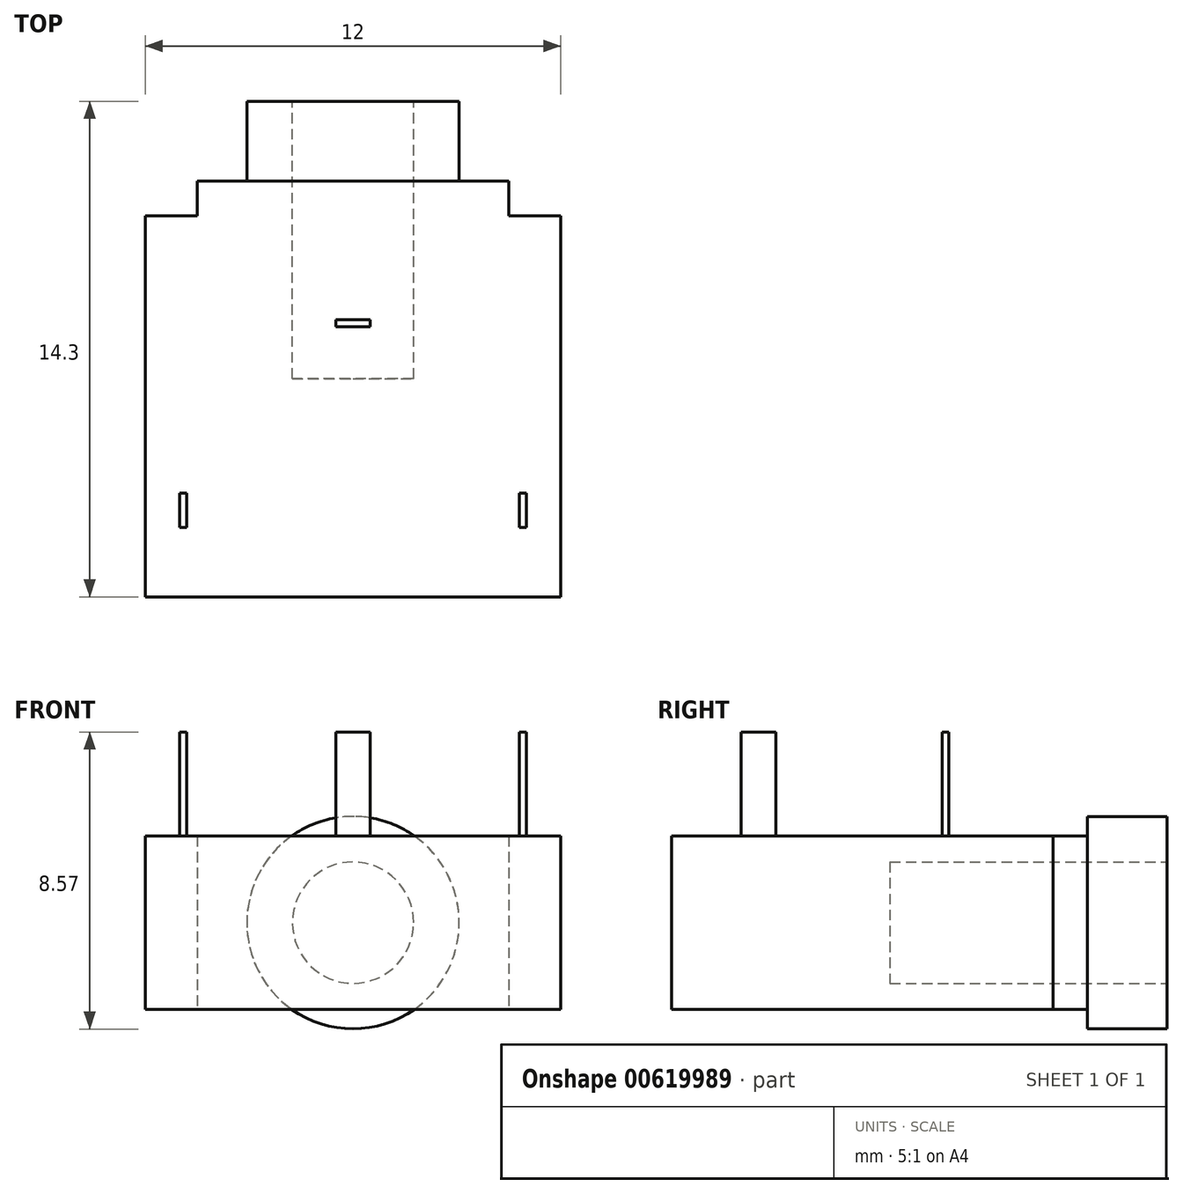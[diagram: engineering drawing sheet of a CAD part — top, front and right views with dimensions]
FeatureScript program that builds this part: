
annotation { "Feature Type Name" : "Feature", "Feature Type Description" : "" }
export const myFeature = defineFeature(function(context is Context, id is Id, definition is map)
    precondition{}
    {
        {
            var Q0;
            Q0=qCreatedBy(makeId("Top.planeOp"),FACE);
            var sketch = newSketch(context, id + "F0", { "sketchPlane" : qUnion([Q0])});
            skLineSegment(sketch, "E0.bottom", {"start": v(6, 5.5) * mm, "end": v(4.5, 5.5) * mm});
            skLineSegment(sketch, "E0.top", {"start": v(6, -5.5) * mm, "end": v(-6, -5.5) * mm});
            skLineSegment(sketch, "E0.left", {"start": v(6, 5.5) * mm, "end": v(6, -5.5) * mm});
            skLineSegment(sketch, "E0.right", {"start": v(-6, 5.5) * mm, "end": v(-6, -5.5) * mm});
            skPoint(sketch, "E0.middle", {"position": v(0, 0) * mm});
            skLineSegment(sketch, "E1", {"start": v(-4.5, 5.5) * mm, "end": v(-4.5, 6.5) * mm});
            skLineSegment(sketch, "E2", {"start": v(-4.5, 6.5) * mm, "end": v(4.5, 6.5) * mm});
            skLineSegment(sketch, "E3", {"start": v(4.5, 6.5) * mm, "end": v(4.5, 5.5) * mm});
            skLineSegment(sketch, "E4.trimOffspring", {"start": v(-4.5, 5.5) * mm, "end": v(-6, 5.5) * mm});
            skSolve(sketch);
        }
        {
            var Q0;
            Q0 = qSketchRegion(id + "F0", true);
            extrude(context, id + "F1", {"entities" : qUnion([Q0]), "depth" : 5 * mm, "offsetDistance" : 25 * mm});
        }
        {
            var Q0;
            Q0=makeQuery(id+"F1.opExtrude","SWEPT_FACE",FACE,{"disambiguationData":[OSD([sQuery(id+"F0.wireOp",EDGE,"E2")])]});
            var sketch = newSketch(context, id + "F2", { "sketchPlane" : qUnion([Q0])});
            skCircle(sketch, "E5", {"center": v(0, 2.5) * mm, "radius": 3.06 * mm});
            skSolve(sketch);
        }
        {
            var Q0;
            Q0 = qSketchRegion(id + "F2", true);
            extrude(context, id + "F3", {"entities" : qUnion([Q0]), "operationType" : NewBodyOperationType.ADD, "depth" : 2.3 * mm, "offsetDistance" : 25 * mm});
        }
        {
            var Q0;
            Q0=makeQuery(id+"F3.opExtrude","CAP_FACE",FACE,{"disambiguationData":[OSD([sQuery(id+"F2.wireOp",EDGE,"E5")])],"isStart":false});
            var sketch = newSketch(context, id + "F4", { "sketchPlane" : qUnion([Q0])});
            skCircle(sketch, "E6", {"center": v(0, 2.5) * mm, "radius": 1.75 * mm});
            skSolve(sketch);
        }
        {
            var Q0;
            Q0 = qSketchRegion(id + "F4", true);
            extrude(context, id + "F5", {"entities" : qUnion([Q0]), "operationType" : NewBodyOperationType.REMOVE, "oppositeDirection" : true, "depth" : 8 * mm, "offsetDistance" : 25 * mm});
        }
        {
            var Q0;
            Q0=makeQuery(id+"F1.opExtrude","CAP_FACE",FACE,{"disambiguationData":[OSD([sQuery(id+"F0.wireOp",EDGE,"E0.bottom"),sQuery(id+"F0.wireOp",EDGE,"E0.top"),sQuery(id+"F0.wireOp",EDGE,"E0.left"),sQuery(id+"F0.wireOp",EDGE,"E0.right"),sQuery(id+"F0.wireOp",EDGE,"E1"),sQuery(id+"F0.wireOp",EDGE,"E2"),sQuery(id+"F0.wireOp",EDGE,"E3"),sQuery(id+"F0.wireOp",EDGE,"E4.trimOffspring")])],"isStart":false});
            var sketch = newSketch(context, id + "F6", { "sketchPlane" : qUnion([Q0])});
            skLineSegment(sketch, "E7.bottom", {"start": v(5, -3.5) * mm, "end": v(4.8, -3.5) * mm});
            skLineSegment(sketch, "E7.top", {"start": v(5, -2.5) * mm, "end": v(4.8, -2.5) * mm});
            skLineSegment(sketch, "E7.left", {"start": v(5, -3.5) * mm, "end": v(5, -2.5) * mm});
            skLineSegment(sketch, "E7.right", {"start": v(4.8, -3.5) * mm, "end": v(4.8, -2.5) * mm});
            skLineSegment(sketch, "E8.bottom", {"start": v(-4.8, -2.5) * mm, "end": v(-5, -2.5) * mm});
            skLineSegment(sketch, "E8.top", {"start": v(-4.8, -3.5) * mm, "end": v(-5, -3.5) * mm});
            skLineSegment(sketch, "E8.left", {"start": v(-4.8, -2.5) * mm, "end": v(-4.8, -3.5) * mm});
            skLineSegment(sketch, "E8.right", {"start": v(-5, -2.5) * mm, "end": v(-5, -3.5) * mm});
            skLineSegment(sketch, "E9.bottom", {"start": v(0.5, 2.5) * mm, "end": v(-0.5, 2.5) * mm});
            skLineSegment(sketch, "E9.top", {"start": v(0.5, 2.3) * mm, "end": v(-0.5, 2.3) * mm});
            skLineSegment(sketch, "E9.left", {"start": v(0.5, 2.5) * mm, "end": v(0.5, 2.3) * mm});
            skLineSegment(sketch, "E9.right", {"start": v(-0.5, 2.5) * mm, "end": v(-0.5, 2.3) * mm});
            skPoint(sketch, "E9.middle", {"position": v(0, 2.4) * mm});
            skSolve(sketch);
        }
        {
            var Q0;
            Q0 = qSketchRegion(id + "F6", true);
            extrude(context, id + "F7", {"entities" : qUnion([Q0]), "operationType" : NewBodyOperationType.ADD, "depth" : 3 * mm, "offsetDistance" : 25 * mm});
        }
    });
